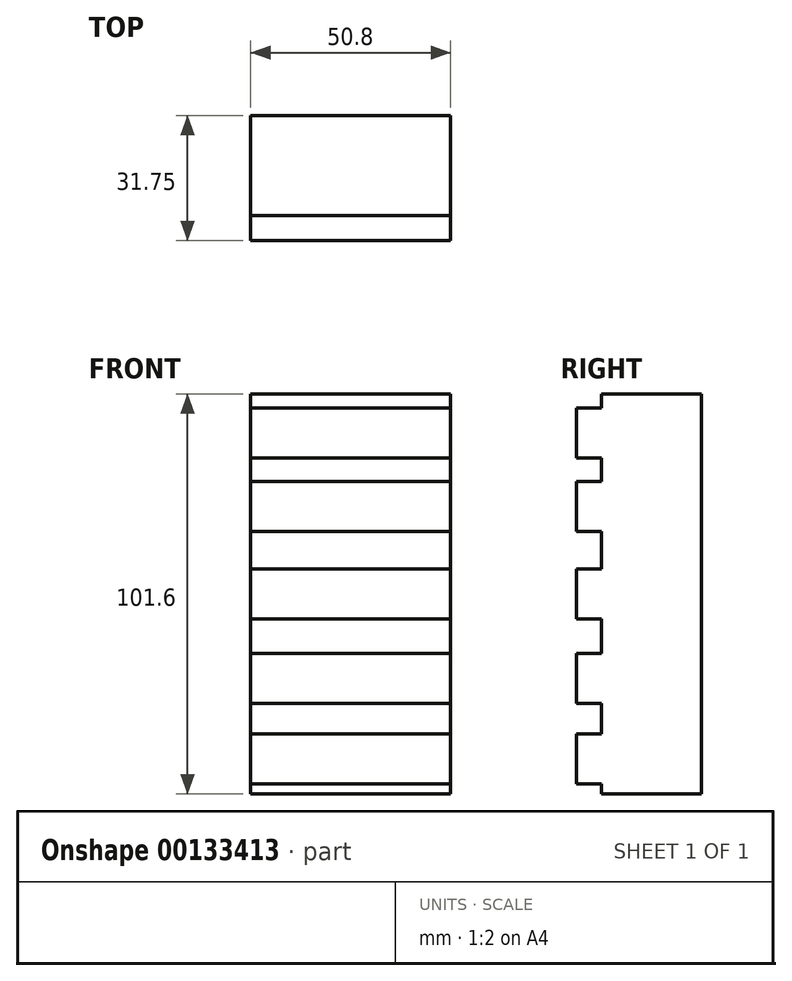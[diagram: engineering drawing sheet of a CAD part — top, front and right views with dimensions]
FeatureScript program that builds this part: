
annotation { "Feature Type Name" : "Feature", "Feature Type Description" : "" }
export const myFeature = defineFeature(function(context is Context, id is Id, definition is map)
    precondition{}
    {
        {
            var Q0;
            Q0=qCreatedBy(makeId("Front.planeOp"),FACE);
            var sketch = newSketch(context, id + "F0", { "sketchPlane" : qUnion([Q0])});
            skLineSegment(sketch, "E0.bottom", {"start": v(-25.4, 50.8) * mm, "end": v(25.4, 50.8) * mm});
            skLineSegment(sketch, "E0.top", {"start": v(-25.4, -50.8) * mm, "end": v(25.4, -50.8) * mm});
            skLineSegment(sketch, "E0.left", {"start": v(-25.4, 50.8) * mm, "end": v(-25.4, -50.8) * mm});
            skLineSegment(sketch, "E0.right", {"start": v(25.4, 50.8) * mm, "end": v(25.4, -50.8) * mm});
            skPoint(sketch, "E0.middle", {"position": v(0, 0) * mm});
            skSolve(sketch);
        }
        {
            var Q0;
            Q0 = qSketchRegion(id + "F0", true);
            extrude(context, id + "F1", {"entities" : qUnion([Q0]), "depth" : 25.4 * mm});
        }
        {
            var Q0;
            Q0=makeQuery(id+"F1.opExtrude","CAP_FACE",FACE,{"disambiguationData":[OSD([sQuery(id+"F0.wireOp",EDGE,"E0.bottom"),sQuery(id+"F0.wireOp",EDGE,"E0.top"),sQuery(id+"F0.wireOp",EDGE,"E0.left"),sQuery(id+"F0.wireOp",EDGE,"E0.right")])],"isStart":false});
            var sketch = newSketch(context, id + "F2", { "sketchPlane" : qUnion([Q0])});
            skLineSegment(sketch, "E1.bottom", {"start": v(-25.4, 6.35) * mm, "end": v(25.4, 6.35) * mm});
            skLineSegment(sketch, "E1.top", {"start": v(-25.4, -6.35) * mm, "end": v(25.4, -6.35) * mm});
            skLineSegment(sketch, "E1.left", {"start": v(-25.4, 6.35) * mm, "end": v(-25.4, -6.35) * mm});
            skLineSegment(sketch, "E1.right", {"start": v(25.4, 6.35) * mm, "end": v(25.4, -6.35) * mm});
            skPoint(sketch, "E1.middle", {"position": v(0, 0) * mm});
            skSolve(sketch);
        }
        {
            var Q0;
            Q0 = qSketchRegion(id + "F2", true);
            extrude(context, id + "F3", {"entities" : qUnion([Q0]), "operationType" : NewBodyOperationType.ADD, "depth" : 6.35 * mm});
        }
        {
            var Q0;
            {var subQ0=sQuery(id+"F0.wireOp",EDGE,"E0.right");var subQ1=sQuery(id+"F0.wireOp",EDGE,"E0.left");var subQ2=sQuery(id+"F0.wireOp",EDGE,"E0.bottom");Q0=makeQuery(id+"F3.boolean.opBoolean","SPLIT",FACE,{"disambiguationData":[TD([makeQuery(id+"F1.opExtrude","SWEPT_FACE",FACE,{"disambiguationData":[OSD([subQ2])]})])],"derivedFrom":makeQuery(id+"F1.opExtrude","CAP_FACE",FACE,{"disambiguationData":[OSD([subQ2,sQuery(id+"F0.wireOp",EDGE,"E0.top"),subQ1,subQ0])],"isStart":false})});}
            var sketch = newSketch(context, id + "F4", { "sketchPlane" : qUnion([Q0])});
            skLineSegment(sketch, "E2.bottom", {"start": v(-25.4, 28.57) * mm, "end": v(25.4, 28.57) * mm});
            skLineSegment(sketch, "E2.top", {"start": v(-25.4, 15.88) * mm, "end": v(25.4, 15.88) * mm});
            skLineSegment(sketch, "E2.left", {"start": v(-25.4, 28.57) * mm, "end": v(-25.4, 15.88) * mm});
            skLineSegment(sketch, "E2.right", {"start": v(25.4, 28.57) * mm, "end": v(25.4, 15.88) * mm});
            skPoint(sketch, "E2.middle", {"position": v(0, 22.22) * mm});
            skLineSegment(sketch, "E3.bottom", {"start": v(-25.4, 47.25) * mm, "end": v(25.4, 47.25) * mm});
            skLineSegment(sketch, "E3.top", {"start": v(-25.4, 34.55) * mm, "end": v(25.4, 34.55) * mm});
            skLineSegment(sketch, "E3.left", {"start": v(-25.4, 47.25) * mm, "end": v(-25.4, 34.55) * mm});
            skLineSegment(sketch, "E3.right", {"start": v(25.4, 47.25) * mm, "end": v(25.4, 34.55) * mm});
            skPoint(sketch, "E3.middle", {"position": v(0, 40.9) * mm});
            skLineSegment(sketch, "E4.bottom", {"start": v(-25.4, -15.12) * mm, "end": v(25.4, -15.12) * mm});
            skLineSegment(sketch, "E4.top", {"start": v(-25.4, -27.82) * mm, "end": v(25.4, -27.82) * mm});
            skLineSegment(sketch, "E4.left", {"start": v(-25.4, -15.12) * mm, "end": v(-25.4, -27.82) * mm});
            skLineSegment(sketch, "E4.right", {"start": v(25.4, -15.12) * mm, "end": v(25.4, -27.82) * mm});
            skPoint(sketch, "E4.middle", {"position": v(0, -21.47) * mm});
            skLineSegment(sketch, "E5.bottom", {"start": v(-25.4, -35.6) * mm, "end": v(25.4, -35.6) * mm});
            skLineSegment(sketch, "E5.top", {"start": v(-25.4, -48.3) * mm, "end": v(25.4, -48.3) * mm});
            skLineSegment(sketch, "E5.left", {"start": v(-25.4, -35.6) * mm, "end": v(-25.4, -48.3) * mm});
            skLineSegment(sketch, "E5.right", {"start": v(25.4, -35.6) * mm, "end": v(25.4, -48.3) * mm});
            skPoint(sketch, "E5.middle", {"position": v(0, -41.95) * mm});
            skSolve(sketch);
        }
        {
            var Q0;
            Q0 = qSketchRegion(id + "F4", true);
            extrude(context, id + "F5", {"entities" : qUnion([Q0]), "operationType" : NewBodyOperationType.ADD, "depth" : 6.35 * mm});
        }
    });
